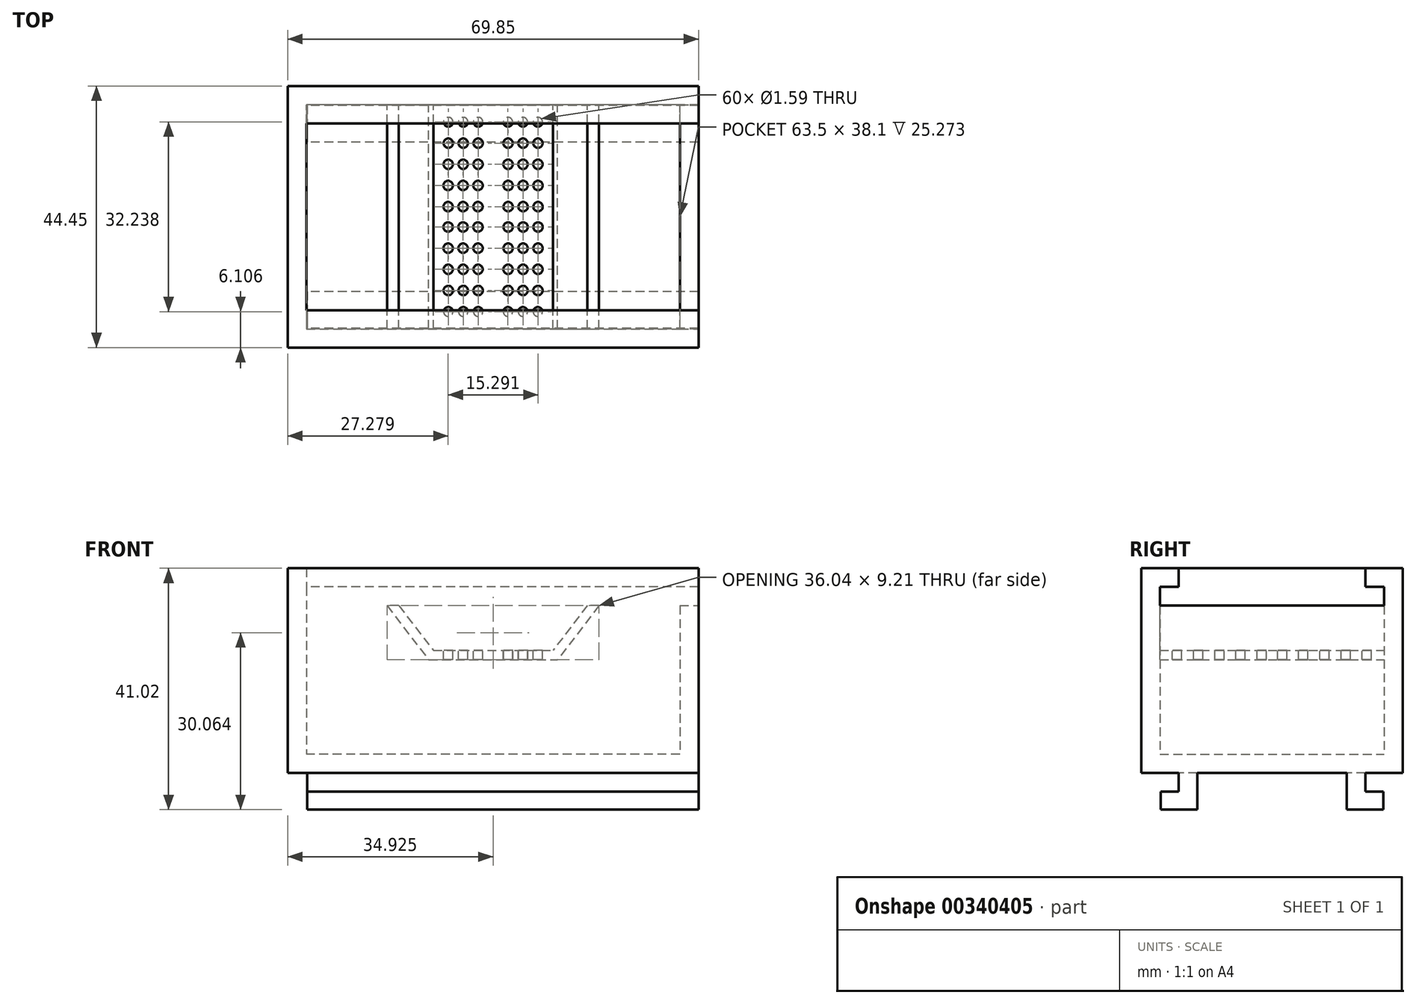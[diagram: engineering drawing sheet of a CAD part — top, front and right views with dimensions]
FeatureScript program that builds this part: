
annotation { "Feature Type Name" : "Feature", "Feature Type Description" : "" }
export const myFeature = defineFeature(function(context is Context, id is Id, definition is map)
    precondition{}
    {
        {
            var Q0;
            Q0=qCreatedBy(makeId("Top.planeOp"),FACE);
            var sketch = newSketch(context, id + "F0", { "sketchPlane" : qUnion([Q0])});
            skLineSegment(sketch, "E0.bottom", {"start": v(0, 0) * mm, "end": v(69.85, 0) * mm});
            skLineSegment(sketch, "E0.top", {"start": v(0, -44.45) * mm, "end": v(69.85, -44.45) * mm});
            skLineSegment(sketch, "E0.left", {"start": v(0, 0) * mm, "end": v(0, -44.45) * mm});
            skLineSegment(sketch, "E0.right", {"start": v(69.85, 0) * mm, "end": v(69.85, -44.45) * mm});
            skSolve(sketch);
        }
        {
            var Q0;
            Q0=makeQuery(id+"F0.imprint","IMPRINT",FACE,{"disambiguationData":[TD([[makeQuery(id+"F0.imprint","IMPRINT",EDGE,{"derivedFrom":sQuery(id+"F0.wireOp",EDGE,"E0.bottom")}),-1.0]])]});
            extrude(context, id + "F1", {"entities" : qUnion([Q0]), "depth" : 3.17 * mm});
        }
        {
            var Q0;
            Q0=makeQuery(id+"F1.opExtrude","CAP_FACE",FACE,{"disambiguationData":[OSD([sQuery(id+"F0.wireOp",EDGE,"E0.bottom"),sQuery(id+"F0.wireOp",EDGE,"E0.top"),sQuery(id+"F0.wireOp",EDGE,"E0.left"),sQuery(id+"F0.wireOp",EDGE,"E0.right")])],"isStart":false});
            var sketch = newSketch(context, id + "F2", { "sketchPlane" : qUnion([Q0])});
            skLineSegment(sketch, "E1.0", {"start": v(3.18, -3.18) * mm, "end": v(3.18, -41.28) * mm});
            skLineSegment(sketch, "E1.1", {"start": v(66.68, -3.18) * mm, "end": v(3.17, -3.18) * mm});
            skLineSegment(sketch, "E1.2", {"start": v(66.68, -41.28) * mm, "end": v(66.68, -3.18) * mm});
            skLineSegment(sketch, "E1.3", {"start": v(3.17, -41.28) * mm, "end": v(66.68, -41.28) * mm});
            skSolve(sketch);
        }
        {
            var Q0;
            Q0=makeQuery(id+"F2.imprint","IMPRINT",FACE,{"disambiguationData":[TD([[makeQuery(id+"F2.imprint","IMPRINT",EDGE,{"derivedFrom":sQuery(id+"F2.wireOp",EDGE,"E1.0")}),-1.0]])]});
            extrude(context, id + "F3", {"entities" : qUnion([Q0]), "operationType" : NewBodyOperationType.ADD, "depth" : 25.27 * mm});
        }
        {
            var Q0;
            Q0=makeQuery(id+"F3.opExtrude","SWEPT_FACE",FACE,{"disambiguationData":[OSD([sQuery(id+"F2.wireOp",EDGE,"E1.1")])]});
            var sketch = newSketch(context, id + "F4", { "sketchPlane" : qUnion([Q0])});
            skLineSegment(sketch, "E2", {"start": v(34.93, 28.45) * mm, "end": v(34.93, 3.18) * mm});
            skPoint(sketch, "E2.endSnap0", {"position": v(34.93, 28.45) * mm});
            skLineSegment(sketch, "E3", {"start": v(18.9, 28.45) * mm, "end": v(24.77, 20.83) * mm});
            skLineSegment(sketch, "E4", {"start": v(24.77, 20.83) * mm, "end": v(34.93, 20.83) * mm});
            skLineSegment(sketch, "E5.MirrorCS", {"start": v(50.94, 28.45) * mm, "end": v(45.09, 20.83) * mm});
            skLineSegment(sketch, "E6.MirrorCS", {"start": v(45.09, 20.83) * mm, "end": v(34.93, 20.83) * mm});
            skLineSegment(sketch, "E7.0", {"start": v(16.9, 28.45) * mm, "end": v(23.98, 19.24) * mm});
            skLineSegment(sketch, "E7.1", {"start": v(23.98, 19.24) * mm, "end": v(33.27, 19.24) * mm});
            skLineSegment(sketch, "E7.2", {"start": v(45.87, 19.24) * mm, "end": v(33.27, 19.24) * mm});
            skLineSegment(sketch, "E7.3", {"start": v(52.94, 28.45) * mm, "end": v(45.87, 19.24) * mm});
            skLineSegment(sketch, "E8", {"start": v(16.9, 28.45) * mm, "end": v(18.9, 28.45) * mm});
            skLineSegment(sketch, "E9", {"start": v(50.94, 28.45) * mm, "end": v(52.94, 28.45) * mm});
            skSolve(sketch);
        }
        {
            var Q0;
            Q0=makeQuery(id+"F4.imprint","IMPRINT",FACE,{"disambiguationData":[TD([[makeQuery(id+"F4.imprint","IMPRINT",EDGE,{"derivedFrom":sQuery(id+"F4.wireOp",EDGE,"E3")}),-1.0]])]});
            var Q1;
            Q1=makeQuery(id+"F4.imprint","IMPRINT",FACE,{"disambiguationData":[TD([[makeQuery(id+"F4.imprint","IMPRINT",EDGE,{"derivedFrom":sQuery(id+"F4.wireOp",EDGE,"E5.MirrorCS")}),1.0]])]});
            extrude(context, id + "F5", {"entities" : qUnion([Q0, Q1]), "operationType" : NewBodyOperationType.ADD, "endBound" : BoundingType.UP_TO_NEXT, "depth" : 25.4 * mm});
        }
        {
            var Q0;
            Q0=makeQuery(id+"F5.opExtrude","SWEPT_FACE",FACE,{"disambiguationData":[OSD([sQuery(id+"F4.wireOp",EDGE,"E4"),sQuery(id+"F4.wireOp",EDGE,"E6.MirrorCS")])]});
            var sketch = newSketch(context, id + "F6", { "sketchPlane" : qUnion([Q0])});
            skLineSegment(sketch, "E10", {"start": v(34.92, -3.17) * mm, "end": v(34.92, -41.27) * mm});
            skLineSegment(sketch, "E11", {"start": v(45.09, -22.23) * mm, "end": v(24.76, -22.23) * mm});
            skLineSegment(sketch, "E12.MirrorCS", {"start": v(24.76, -22.23) * mm, "end": v(45.09, -22.23) * mm});
            skCircle(sketch, "E13", {"center": v(27.31, -6.1) * mm, "radius": 0.8 * mm});
            skCircle(sketch, "E14.1.0.0", {"center": v(29.85, -6.1) * mm, "radius": 0.8 * mm});
            skCircle(sketch, "E14.2.0.0", {"center": v(32.4, -6.1) * mm, "radius": 0.8 * mm});
            skLineSegment(sketch, "E14.direction1", {"start": v(27.31, -6.1) * mm, "end": v(29.85, -6.1) * mm, "construction": true});
            skCircle(sketch, "E15.1.0.0", {"center": v(27.3, -9.7) * mm, "radius": 0.8 * mm});
            skCircle(sketch, "E15.1.0.1", {"center": v(29.84, -9.7) * mm, "radius": 0.8 * mm});
            skCircle(sketch, "E15.1.0.2", {"center": v(32.38, -9.7) * mm, "radius": 0.8 * mm});
            skCircle(sketch, "E15.2.0.0", {"center": v(27.3, -13.3) * mm, "radius": 0.8 * mm});
            skCircle(sketch, "E15.2.0.1", {"center": v(29.84, -13.3) * mm, "radius": 0.8 * mm});
            skCircle(sketch, "E15.2.0.2", {"center": v(32.38, -13.3) * mm, "radius": 0.8 * mm});
            skCircle(sketch, "E15.3.0.0", {"center": v(27.29, -16.9) * mm, "radius": 0.8 * mm});
            skCircle(sketch, "E15.3.0.1", {"center": v(29.83, -16.9) * mm, "radius": 0.8 * mm});
            skCircle(sketch, "E15.3.0.2", {"center": v(32.37, -16.9) * mm, "radius": 0.8 * mm});
            skCircle(sketch, "E15.4.0.0", {"center": v(27.28, -20.5) * mm, "radius": 0.8 * mm});
            skCircle(sketch, "E15.4.0.1", {"center": v(29.82, -20.5) * mm, "radius": 0.8 * mm});
            skCircle(sketch, "E15.4.0.2", {"center": v(32.36, -20.5) * mm, "radius": 0.8 * mm});
            skLineSegment(sketch, "E15.direction1", {"start": v(27.31, -6.1) * mm, "end": v(27.3, -9.7) * mm, "construction": true});
            skCircle(sketch, "E16.MirrorC", {"center": v(42.54, -6.1) * mm, "radius": 0.8 * mm});
            skCircle(sketch, "E17.MirrorC", {"center": v(40, -6.1) * mm, "radius": 0.8 * mm});
            skCircle(sketch, "E18.MirrorC", {"center": v(37.46, -6.1) * mm, "radius": 0.8 * mm});
            skCircle(sketch, "E19.MirrorC", {"center": v(37.46, -9.7) * mm, "radius": 0.8 * mm});
            skCircle(sketch, "E20.MirrorC", {"center": v(40, -9.7) * mm, "radius": 0.8 * mm});
            skCircle(sketch, "E21.MirrorC", {"center": v(42.55, -9.7) * mm, "radius": 0.8 * mm});
            skCircle(sketch, "E22.MirrorC", {"center": v(42.55, -13.3) * mm, "radius": 0.8 * mm});
            skCircle(sketch, "E23.MirrorC", {"center": v(40.01, -13.3) * mm, "radius": 0.8 * mm});
            skCircle(sketch, "E24.MirrorC", {"center": v(37.47, -13.3) * mm, "radius": 0.8 * mm});
            skCircle(sketch, "E25.MirrorC", {"center": v(42.56, -16.9) * mm, "radius": 0.8 * mm});
            skCircle(sketch, "E26.MirrorC", {"center": v(40.02, -16.9) * mm, "radius": 0.8 * mm});
            skCircle(sketch, "E27.MirrorC", {"center": v(37.48, -16.9) * mm, "radius": 0.8 * mm});
            skCircle(sketch, "E28.MirrorC", {"center": v(42.57, -20.5) * mm, "radius": 0.8 * mm});
            skCircle(sketch, "E29.MirrorC", {"center": v(40.03, -20.5) * mm, "radius": 0.8 * mm});
            skCircle(sketch, "E30.MirrorC", {"center": v(37.5, -20.5) * mm, "radius": 0.8 * mm});
            skCircle(sketch, "E31.MirrorC", {"center": v(27.28, -23.96) * mm, "radius": 0.8 * mm});
            skCircle(sketch, "E32.MirrorC", {"center": v(29.82, -23.96) * mm, "radius": 0.8 * mm});
            skCircle(sketch, "E33.MirrorC", {"center": v(32.36, -23.96) * mm, "radius": 0.8 * mm});
            skCircle(sketch, "E34.MirrorC", {"center": v(27.29, -27.55) * mm, "radius": 0.8 * mm});
            skCircle(sketch, "E35.MirrorC", {"center": v(29.83, -27.55) * mm, "radius": 0.8 * mm});
            skCircle(sketch, "E36.MirrorC", {"center": v(32.37, -27.55) * mm, "radius": 0.8 * mm});
            skCircle(sketch, "E37.MirrorC", {"center": v(32.38, -31.15) * mm, "radius": 0.8 * mm});
            skCircle(sketch, "E38.MirrorC", {"center": v(29.84, -31.15) * mm, "radius": 0.8 * mm});
            skCircle(sketch, "E39.MirrorC", {"center": v(27.3, -31.15) * mm, "radius": 0.8 * mm});
            skCircle(sketch, "E40.MirrorC", {"center": v(27.3, -34.75) * mm, "radius": 0.8 * mm});
            skCircle(sketch, "E41.MirrorC", {"center": v(29.85, -34.75) * mm, "radius": 0.8 * mm});
            skCircle(sketch, "E42.MirrorC", {"center": v(32.39, -34.75) * mm, "radius": 0.8 * mm});
            skCircle(sketch, "E43.MirrorC", {"center": v(32.4, -38.34) * mm, "radius": 0.8 * mm});
            skCircle(sketch, "E44.MirrorC", {"center": v(29.85, -38.34) * mm, "radius": 0.8 * mm});
            skCircle(sketch, "E45.MirrorC", {"center": v(27.31, -38.34) * mm, "radius": 0.8 * mm});
            skCircle(sketch, "E46.MirrorC", {"center": v(37.46, -38.34) * mm, "radius": 0.8 * mm});
            skCircle(sketch, "E47.MirrorC", {"center": v(40, -38.34) * mm, "radius": 0.8 * mm});
            skCircle(sketch, "E48.MirrorC", {"center": v(42.54, -38.34) * mm, "radius": 0.8 * mm});
            skCircle(sketch, "E49.MirrorC", {"center": v(37.47, -34.75) * mm, "radius": 0.8 * mm});
            skCircle(sketch, "E50.MirrorC", {"center": v(40, -34.75) * mm, "radius": 0.8 * mm});
            skCircle(sketch, "E51.MirrorC", {"center": v(42.55, -34.75) * mm, "radius": 0.8 * mm});
            skCircle(sketch, "E52.MirrorC", {"center": v(37.47, -31.15) * mm, "radius": 0.8 * mm});
            skCircle(sketch, "E53.MirrorC", {"center": v(40.01, -31.15) * mm, "radius": 0.8 * mm});
            skCircle(sketch, "E54.MirrorC", {"center": v(42.55, -31.15) * mm, "radius": 0.8 * mm});
            skCircle(sketch, "E55.MirrorC", {"center": v(37.48, -27.55) * mm, "radius": 0.8 * mm});
            skCircle(sketch, "E56.MirrorC", {"center": v(40.02, -27.55) * mm, "radius": 0.8 * mm});
            skCircle(sketch, "E57.MirrorC", {"center": v(42.56, -27.55) * mm, "radius": 0.8 * mm});
            skCircle(sketch, "E58.MirrorC", {"center": v(37.5, -23.96) * mm, "radius": 0.8 * mm});
            skCircle(sketch, "E59.MirrorC", {"center": v(40.03, -23.96) * mm, "radius": 0.8 * mm});
            skCircle(sketch, "E60.MirrorC", {"center": v(42.57, -23.96) * mm, "radius": 0.8 * mm});
            skSolve(sketch);
        }
        {
            var Q0;
            Q0 = qSketchRegion(id + "F6", true);
            extrude(context, id + "F7", {"entities" : qUnion([Q0]), "operationType" : NewBodyOperationType.REMOVE, "endBound" : BoundingType.UP_TO_NEXT, "oppositeDirection" : true, "depth" : 25.4 * mm});
        }
        {
            var Q0;
            Q0=makeQuery(id+"F5.boolean.opBoolean","MERGE",FACE,{"derivedFrom":[makeQuery(id+"F3.opExtrude","CAP_FACE",FACE,{"disambiguationData":[OSD([sQuery(id+"F0.wireOp",EDGE,"E0.bottom"),sQuery(id+"F0.wireOp",EDGE,"E0.top"),sQuery(id+"F0.wireOp",EDGE,"E0.left"),sQuery(id+"F0.wireOp",EDGE,"E0.right"),sQuery(id+"F2.wireOp",EDGE,"E1.0"),sQuery(id+"F2.wireOp",EDGE,"E1.1"),sQuery(id+"F2.wireOp",EDGE,"E1.2"),sQuery(id+"F2.wireOp",EDGE,"E1.3")])],"isStart":false}),makeQuery(id+"F5.opExtrude","SWEPT_FACE",FACE,{"disambiguationData":[OSD([sQuery(id+"F4.wireOp",EDGE,"E8")])]}),makeQuery(id+"F5.opExtrude","SWEPT_FACE",FACE,{"disambiguationData":[OSD([sQuery(id+"F4.wireOp",EDGE,"E9")])]})]});
            var sketch = newSketch(context, id + "F8", { "sketchPlane" : qUnion([Q0])});
            skLineSegment(sketch, "E61", {"start": v(16.9, -41.28) * mm, "end": v(18.9, -41.28) * mm});
            skLineSegment(sketch, "E62", {"start": v(50.94, -41.28) * mm, "end": v(52.94, -41.28) * mm});
            skLineSegment(sketch, "E63", {"start": v(52.94, -3.18) * mm, "end": v(50.94, -3.18) * mm});
            skLineSegment(sketch, "E64", {"start": v(18.9, -3.18) * mm, "end": v(16.9, -3.18) * mm});
            skSolve(sketch);
        }
        {
            var Q0;
            Q0 = qSketchRegion(id + "F8", true);
            var Q1;
            Q1=makeQuery(id+"F8.imprint","IMPRINT",FACE,{"disambiguationData":[TD([[makeQuery(id+"F8.imprint","IMPRINT",EDGE,{"derivedFrom":sQuery(id+"F8.wireOp",EDGE,"E61")}),-1.0]])]});
            extrude(context, id + "F9", {"entities" : qUnion([Q0, Q1]), "operationType" : NewBodyOperationType.ADD, "depth" : 6.35 * mm});
        }
        {
            var Q0;
            {var subQ0=sQuery(id+"F2.wireOp",EDGE,"E1.3");var subQ2=sQuery(id+"F2.wireOp",EDGE,"E1.0");var subQ10=makeQuery(id+"F3.opExtrude","SWEPT_FACE",FACE,{"disambiguationData":[OSD([subQ0])]});Q0=makeQuery(id+"F9.boolean.opBoolean","MERGE",FACE,{"derivedFrom":[makeQuery(id+"F5.boolean.opBoolean","SPLIT",FACE,{"disambiguationData":[TD([makeQuery(id+"F5.opExtrude","SWEPT_FACE",FACE,{"disambiguationData":[OSD([sQuery(id+"F4.wireOp",EDGE,"E3")])]})])],"derivedFrom":subQ10}),makeQuery(id+"F5.boolean.opBoolean","SPLIT",FACE,{"disambiguationData":[TD([makeQuery(id+"F3.opExtrude","SWEPT_FACE",FACE,{"disambiguationData":[OSD([subQ2])]})])],"derivedFrom":subQ10}),makeQuery(id+"F9.opExtrude","SWEPT_FACE",FACE,{"disambiguationData":[OSD([subQ0,sQuery(id+"F8.wireOp",EDGE,"E61"),sQuery(id+"F8.wireOp",EDGE,"E62")])]})]});}
            var sketch = newSketch(context, id + "F10", { "sketchPlane" : qUnion([Q0])});
            skLineSegment(sketch, "E65.bottom", {"start": v(-66.68, 34.8) * mm, "end": v(-3.17, 34.8) * mm});
            skLineSegment(sketch, "E65.top", {"start": v(-66.68, 31.62) * mm, "end": v(-3.17, 31.62) * mm});
            skLineSegment(sketch, "E65.left", {"start": v(-66.68, 34.8) * mm, "end": v(-66.68, 31.62) * mm});
            skLineSegment(sketch, "E65.right", {"start": v(-3.18, 34.8) * mm, "end": v(-3.18, 31.62) * mm});
            skSolve(sketch);
        }
        {
            var Q0;
            Q0=makeQuery(id+"F10.imprint","IMPRINT",FACE,{"disambiguationData":[TD([[makeQuery(id+"F10.imprint","IMPRINT",EDGE,{"derivedFrom":sQuery(id+"F10.wireOp",EDGE,"E65.bottom")}),1.0]])]});
            extrude(context, id + "F11", {"entities" : qUnion([Q0]), "operationType" : NewBodyOperationType.ADD, "depth" : 3.17 * mm});
        }
        {
            var Q0;
            {var subQ0=sQuery(id+"F2.wireOp",EDGE,"E1.1");var subQ2=sQuery(id+"F2.wireOp",EDGE,"E1.0");var subQ10=makeQuery(id+"F3.opExtrude","SWEPT_FACE",FACE,{"disambiguationData":[OSD([subQ0])]});Q0=makeQuery(id+"F9.boolean.opBoolean","MERGE",FACE,{"derivedFrom":[makeQuery(id+"F5.boolean.opBoolean","SPLIT",FACE,{"disambiguationData":[TD([makeQuery(id+"F5.opExtrude","SWEPT_FACE",FACE,{"disambiguationData":[OSD([sQuery(id+"F4.wireOp",EDGE,"E3")])]})])],"derivedFrom":subQ10}),makeQuery(id+"F5.boolean.opBoolean","SPLIT",FACE,{"disambiguationData":[TD([makeQuery(id+"F3.opExtrude","SWEPT_FACE",FACE,{"disambiguationData":[OSD([subQ2])]})])],"derivedFrom":subQ10}),makeQuery(id+"F9.opExtrude","SWEPT_FACE",FACE,{"disambiguationData":[OSD([subQ0,sQuery(id+"F8.wireOp",EDGE,"E63"),sQuery(id+"F8.wireOp",EDGE,"E64")])]})]});}
            var sketch = newSketch(context, id + "F12", { "sketchPlane" : qUnion([Q0])});
            skLineSegment(sketch, "E66.bottom", {"start": v(66.68, 34.8) * mm, "end": v(3.17, 34.8) * mm});
            skLineSegment(sketch, "E66.top", {"start": v(66.68, 31.62) * mm, "end": v(3.17, 31.62) * mm});
            skLineSegment(sketch, "E66.left", {"start": v(66.68, 34.8) * mm, "end": v(66.68, 31.62) * mm});
            skLineSegment(sketch, "E66.right", {"start": v(3.18, 34.8) * mm, "end": v(3.18, 31.62) * mm});
            skSolve(sketch);
        }
        {
            var Q0;
            Q0=makeQuery(id+"F12.imprint","IMPRINT",FACE,{"disambiguationData":[TD([[makeQuery(id+"F12.imprint","IMPRINT",EDGE,{"derivedFrom":sQuery(id+"F12.wireOp",EDGE,"E66.bottom")}),1.0]])]});
            extrude(context, id + "F13", {"entities" : qUnion([Q0]), "operationType" : NewBodyOperationType.ADD, "depth" : 3.17 * mm});
        }
        {
            var Q0;
            {var subQ0=sQuery(id+"F0.wireOp",EDGE,"E0.right");Q0=makeQuery(id+"F9.boolean.opBoolean","MERGE",FACE,{"derivedFrom":[makeQuery(id+"F3.boolean.opBoolean","MERGE",FACE,{"derivedFrom":[makeQuery(id+"F1.opExtrude","SWEPT_FACE",FACE,{"disambiguationData":[OSD([subQ0])]}),makeQuery(id+"F3.opExtrude","SWEPT_FACE",FACE,{"disambiguationData":[OSD([subQ0])]})]}),makeQuery(id+"F9.opExtrude","SWEPT_FACE",FACE,{"disambiguationData":[OSD([subQ0])]})]});}
            var sketch = newSketch(context, id + "F14", { "sketchPlane" : qUnion([Q0])});
            skLineSegment(sketch, "E67.bottom", {"start": v(-38.1, 34.8) * mm, "end": v(-6.35, 34.8) * mm});
            skLineSegment(sketch, "E67.top", {"start": v(-38.1, 31.62) * mm, "end": v(-6.35, 31.62) * mm});
            skLineSegment(sketch, "E67.left", {"start": v(-38.1, 34.8) * mm, "end": v(-38.1, 31.62) * mm});
            skLineSegment(sketch, "E67.right", {"start": v(-6.35, 34.8) * mm, "end": v(-6.35, 31.62) * mm});
            skLineSegment(sketch, "E68.bottom", {"start": v(-41.28, 31.62) * mm, "end": v(-3.18, 31.62) * mm});
            skLineSegment(sketch, "E68.top", {"start": v(-41.28, 28.45) * mm, "end": v(-3.18, 28.45) * mm});
            skLineSegment(sketch, "E68.left", {"start": v(-41.28, 31.62) * mm, "end": v(-41.28, 28.45) * mm});
            skLineSegment(sketch, "E68.right", {"start": v(-3.18, 31.62) * mm, "end": v(-3.18, 28.45) * mm});
            skSolve(sketch);
        }
        {
            var Q0;
            Q0=makeQuery(id+"F14.imprint","IMPRINT",FACE,{"disambiguationData":[TD([[makeQuery(id+"F14.imprint","IMPRINT",EDGE,{"derivedFrom":sQuery(id+"F14.wireOp",EDGE,"E67.bottom")}),1.0]])]});
            var Q1;
            Q1=makeQuery(id+"F14.imprint","IMPRINT",FACE,{"disambiguationData":[TD([[makeQuery(id+"F14.imprint","IMPRINT",EDGE,{"derivedFrom":sQuery(id+"F14.wireOp",EDGE,"E68.top")}),1.0]])]});
            extrude(context, id + "F15", {"entities" : qUnion([Q0, Q1]), "operationType" : NewBodyOperationType.REMOVE, "endBound" : BoundingType.UP_TO_NEXT, "oppositeDirection" : true, "depth" : 25.4 * mm});
        }
        {
            var Q0;
            Q0=makeQuery(id+"F1.opExtrude","CAP_FACE",FACE,{"disambiguationData":[OSD([sQuery(id+"F0.wireOp",EDGE,"E0.bottom"),sQuery(id+"F0.wireOp",EDGE,"E0.top"),sQuery(id+"F0.wireOp",EDGE,"E0.left"),sQuery(id+"F0.wireOp",EDGE,"E0.right")])],"isStart":true});
            var sketch = newSketch(context, id + "F16", { "sketchPlane" : qUnion([Q0])});
            skLineSegment(sketch, "E69.bottom", {"start": v(69.85, 38.1) * mm, "end": v(0, 38.1) * mm});
            skLineSegment(sketch, "E69.top", {"start": v(69.85, 34.93) * mm, "end": v(0, 34.92) * mm});
            skLineSegment(sketch, "E69.left", {"start": v(69.85, 38.1) * mm, "end": v(69.85, 34.93) * mm});
            skLineSegment(sketch, "E69.right", {"start": v(0, 38.1) * mm, "end": v(0, 34.92) * mm});
            skLineSegment(sketch, "E70", {"start": v(69.85, 22.23) * mm, "end": v(0, 22.23) * mm});
            skLineSegment(sketch, "E71.MirrorCS", {"start": v(69.85, 9.53) * mm, "end": v(0, 9.53) * mm});
            skLineSegment(sketch, "E72.MirrorCS", {"start": v(69.85, 6.35) * mm, "end": v(69.85, 9.53) * mm});
            skLineSegment(sketch, "E73.MirrorCS", {"start": v(69.85, 6.35) * mm, "end": v(0, 6.35) * mm});
            skLineSegment(sketch, "E74.MirrorCS", {"start": v(0, 6.35) * mm, "end": v(0, 9.53) * mm});
            skSolve(sketch);
        }
        {
            var Q0;
            Q0=makeQuery(id+"F16.imprint","IMPRINT",FACE,{"disambiguationData":[TD([[makeQuery(id+"F16.imprint","IMPRINT",EDGE,{"derivedFrom":sQuery(id+"F16.wireOp",EDGE,"E71.MirrorCS")}),1.0]])]});
            var Q1;
            Q1=makeQuery(id+"F16.imprint","IMPRINT",FACE,{"disambiguationData":[TD([[makeQuery(id+"F16.imprint","IMPRINT",EDGE,{"derivedFrom":sQuery(id+"F16.wireOp",EDGE,"E69.bottom")}),1.0]])]});
            extrude(context, id + "F17", {"entities" : qUnion([Q0, Q1]), "operationType" : NewBodyOperationType.ADD, "depth" : 6.22 * mm});
        }
        {
            var Q0;
            Q0=makeQuery(id+"F17.opExtrude","SWEPT_FACE",FACE,{"disambiguationData":[OSD([sQuery(id+"F16.wireOp",EDGE,"E69.bottom")])]});
            var sketch = newSketch(context, id + "F18", { "sketchPlane" : qUnion([Q0])});
            skLineSegment(sketch, "E75.bottom", {"start": v(69.85, -6.22) * mm, "end": v(0, -6.22) * mm});
            skLineSegment(sketch, "E75.top", {"start": v(69.85, -3.17) * mm, "end": v(0, -3.18) * mm});
            skLineSegment(sketch, "E75.left", {"start": v(69.85, -6.22) * mm, "end": v(69.85, -3.17) * mm});
            skLineSegment(sketch, "E75.right", {"start": v(0, -6.22) * mm, "end": v(0, -3.18) * mm});
            skSolve(sketch);
        }
        {
            var Q0;
            Q0 = qSketchRegion(id + "F18", true);
            extrude(context, id + "F19", {"entities" : qUnion([Q0]), "operationType" : NewBodyOperationType.ADD, "depth" : 3.05 * mm});
        }
        {
            var Q0;
            Q0=makeQuery(id+"F17.opExtrude","SWEPT_FACE",FACE,{"disambiguationData":[OSD([sQuery(id+"F16.wireOp",EDGE,"E73.MirrorCS")])]});
            var sketch = newSketch(context, id + "F20", { "sketchPlane" : qUnion([Q0])});
            skLineSegment(sketch, "E76.bottom", {"start": v(-69.85, -6.22) * mm, "end": v(0, -6.22) * mm});
            skLineSegment(sketch, "E76.top", {"start": v(-69.85, -3.17) * mm, "end": v(0, -3.17) * mm});
            skLineSegment(sketch, "E76.left", {"start": v(-69.85, -6.22) * mm, "end": v(-69.85, -3.17) * mm});
            skLineSegment(sketch, "E76.right", {"start": v(0, -6.22) * mm, "end": v(0, -3.17) * mm});
            skSolve(sketch);
        }
        {
            var Q0;
            Q0=makeQuery(id+"F20.imprint","IMPRINT",FACE,{"disambiguationData":[TD([[makeQuery(id+"F20.imprint","IMPRINT",EDGE,{"derivedFrom":sQuery(id+"F20.wireOp",EDGE,"E76.bottom")}),1.0]])]});
            extrude(context, id + "F21", {"entities" : qUnion([Q0]), "operationType" : NewBodyOperationType.ADD, "depth" : 3.05 * mm});
        }
        {
            var Q0;
            Q0=makeQuery(id+"F19.opExtrude","CAP_FACE",FACE,{"disambiguationData":[OSD([sQuery(id+"F18.wireOp",EDGE,"E75.bottom"),sQuery(id+"F18.wireOp",EDGE,"E75.top"),sQuery(id+"F18.wireOp",EDGE,"E75.left"),sQuery(id+"F18.wireOp",EDGE,"E75.right")])],"isStart":false});
            var sketch = newSketch(context, id + "F22", { "sketchPlane" : qUnion([Q0])});
            skLineSegment(sketch, "E77.bottom", {"start": v(0, -6.22) * mm, "end": v(3.3, -6.22) * mm});
            skLineSegment(sketch, "E77.top", {"start": v(0, 0) * mm, "end": v(3.3, 0) * mm});
            skLineSegment(sketch, "E77.left", {"start": v(0, -6.22) * mm, "end": v(0, 0) * mm});
            skLineSegment(sketch, "E77.right", {"start": v(3.3, -6.22) * mm, "end": v(3.3, 0) * mm});
            skSolve(sketch);
        }
        {
            var Q0;
            Q0 = qSketchRegion(id + "F22", true);
            extrude(context, id + "F23", {"entities" : qUnion([Q0]), "operationType" : NewBodyOperationType.REMOVE, "oppositeDirection" : true, "depth" : 38.1 * mm});
        }
    });
